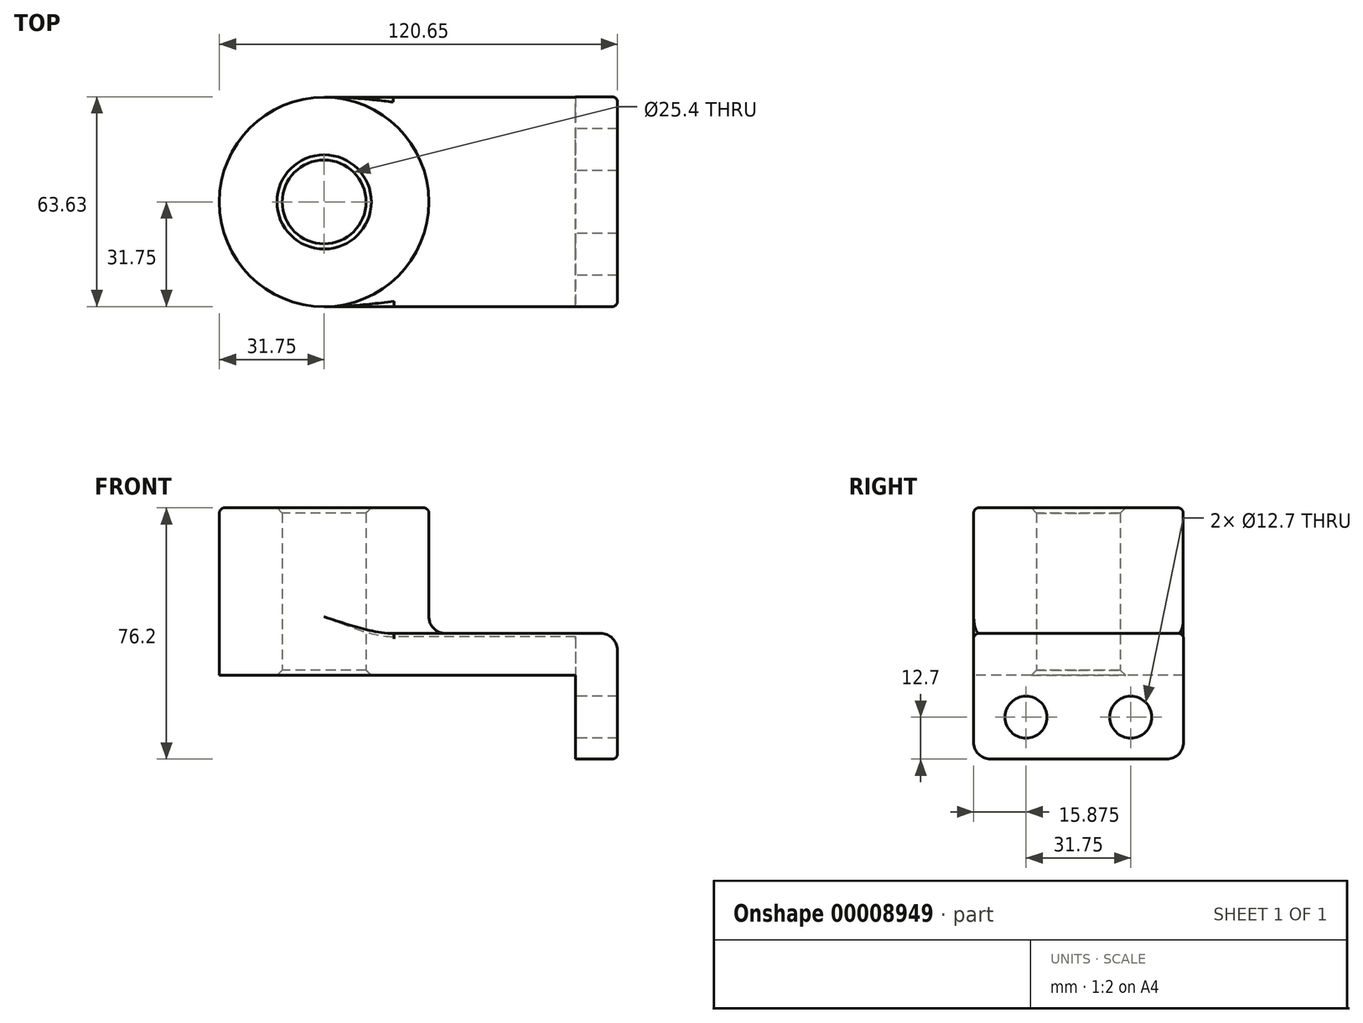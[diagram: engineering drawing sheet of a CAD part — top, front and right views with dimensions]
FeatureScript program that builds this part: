
annotation { "Feature Type Name" : "Feature", "Feature Type Description" : "" }
export const myFeature = defineFeature(function(context is Context, id is Id, definition is map)
    precondition{}
    {
        {
            var Q0;
            Q0=qCreatedBy(makeId("Top.planeOp"),FACE);
            var sketch = newSketch(context, id + "F0", { "sketchPlane" : qUnion([Q0])});
            skLineSegment(sketch, "E0.rect.bottom", {"start": v(-38.1, 31.75) * mm, "end": v(38.1, 31.75) * mm});
            skLineSegment(sketch, "E0.rect.top", {"start": v(-38.1, -31.75) * mm, "end": v(38.1, -31.75) * mm});
            skLineSegment(sketch, "E0.rect.left", {"start": v(-38.1, 31.75) * mm, "end": v(-38.1, -31.75) * mm});
            skLineSegment(sketch, "E0.rect.right", {"start": v(38.1, 31.75) * mm, "end": v(38.1, -31.75) * mm});
            skPoint(sketch, "E0.rect.middle", {"position": v(0, 0) * mm});
            skCircle(sketch, "E1", {"center": v(-38.1, 0) * mm, "radius": 31.75 * mm});
            skCircle(sketch, "E2", {"center": v(-38.1, 0) * mm, "radius": 12.7 * mm});
            skSolve(sketch);
        }
        {
            var Q0;
            {var subQ3=sQuery(id+"F0.wireOp",EDGE,"E0.rect.bottom");Q0=makeQuery(id+"F0.imprint","IMPRINT",FACE,{"disambiguationData":[TD([[makeQuery(id+"F0.imprint","IMPRINT",EDGE,{"derivedFrom":subQ3}),-1.0]])]});}
            var Q1;
            {var subQ0=sQuery(id+"F0.wireOp",EDGE,"E2");var subQ1=sQuery(id+"F0.wireOp",EDGE,"E0.rect.left");var subQ3=makeQuery(id+"F0.imprint","INTERSECT",VERTEX,{"disambiguationData":[OD(0.0)],"derivedFrom":[subQ1,subQ0]});Q1=makeQuery(id+"F0.imprint","IMPRINT",FACE,{"disambiguationData":[TD([[makeQuery(id+"F0.imprint","IMPRINT",EDGE,{"disambiguationData":[TD([[subQ3,1.0]])],"derivedFrom":subQ0}),-1.0]])]});}
            var Q2;
            {var subQ0=sQuery(id+"F0.wireOp",EDGE,"E2");var subQ1=sQuery(id+"F0.wireOp",EDGE,"E0.rect.left");var subQ3=makeQuery(id+"F0.imprint","INTERSECT",VERTEX,{"disambiguationData":[OD(0.0)],"derivedFrom":[subQ1,subQ0]});Q2=makeQuery(id+"F0.imprint","IMPRINT",FACE,{"disambiguationData":[TD([[makeQuery(id+"F0.imprint","IMPRINT",EDGE,{"disambiguationData":[TD([[subQ3,-1.0]])],"derivedFrom":subQ0}),-1.0]])]});}
            extrude(context, id + "F1", {"entities" : qUnion([Q0, Q1, Q2]), "depth" : 12.7 * mm});
        }
        {
            var Q0;
            {var subQ0=sQuery(id+"F0.wireOp",EDGE,"E2");var subQ1=sQuery(id+"F0.wireOp",EDGE,"E0.rect.left");var subQ3=makeQuery(id+"F0.imprint","INTERSECT",VERTEX,{"disambiguationData":[OD(0.0)],"derivedFrom":[subQ1,subQ0]});Q0=makeQuery(id+"F0.imprint","IMPRINT",FACE,{"disambiguationData":[TD([[makeQuery(id+"F0.imprint","IMPRINT",EDGE,{"disambiguationData":[TD([[subQ3,1.0]])],"derivedFrom":subQ0}),-1.0]])]});}
            var Q1;
            {var subQ0=sQuery(id+"F0.wireOp",EDGE,"E2");var subQ1=sQuery(id+"F0.wireOp",EDGE,"E0.rect.left");var subQ3=makeQuery(id+"F0.imprint","INTERSECT",VERTEX,{"disambiguationData":[OD(0.0)],"derivedFrom":[subQ1,subQ0]});Q1=makeQuery(id+"F0.imprint","IMPRINT",FACE,{"disambiguationData":[TD([[makeQuery(id+"F0.imprint","IMPRINT",EDGE,{"disambiguationData":[TD([[subQ3,-1.0]])],"derivedFrom":subQ0}),-1.0]])]});}
            extrude(context, id + "F2", {"entities" : qUnion([Q0, Q1]), "operationType" : NewBodyOperationType.ADD, "depth" : 50.8 * mm});
        }
        {
            var Q0;
            Q0=makeQuery(id+"F1.opExtrude","SWEPT_FACE",FACE,{"disambiguationData":[OSD([sQuery(id+"F0.wireOp",EDGE,"E0.rect.right")])]});
            var sketch = newSketch(context, id + "F3", { "sketchPlane" : qUnion([Q0])});
            skLineSegment(sketch, "E3.bottom", {"start": v(-31.75, 12.7) * mm, "end": v(31.88, 12.7) * mm});
            skLineSegment(sketch, "E3.top", {"start": v(-31.75, -25.4) * mm, "end": v(31.88, -25.4) * mm});
            skLineSegment(sketch, "E3.left", {"start": v(-31.75, 12.7) * mm, "end": v(-31.75, -25.4) * mm});
            skLineSegment(sketch, "E3.right", {"start": v(31.88, 12.7) * mm, "end": v(31.88, -25.4) * mm});
            skLineSegment(sketch, "E4", {"start": v(0, -25.4) * mm, "end": v(0, 0) * mm, "construction": true});
            skCircle(sketch, "E5", {"center": v(-15.87, -12.7) * mm, "radius": 6.35 * mm});
            skCircle(sketch, "E6.MirrorC", {"center": v(15.87, -12.7) * mm, "radius": 6.35 * mm});
            skSolve(sketch);
        }
        {
            var Q0;
            {var subQ5=sQuery(id+"F3.wireOp",EDGE,"E3.top");Q0=makeQuery(id+"F3.imprint","IMPRINT",FACE,{"disambiguationData":[TD([[makeQuery(id+"F3.imprint","IMPRINT",EDGE,{"derivedFrom":subQ5}),1.0]])]});}
            var Q1;
            {var subQ0=sQuery(id+"F0.wireOp",EDGE,"E0.rect.right");var subQ1=makeQuery(id+"F1.opExtrude","CAP_EDGE",EDGE,{"disambiguationData":[OSD([subQ0])],"isStart":true});Q1=makeQuery(id+"F3.imprint","IMPRINT",FACE,{"disambiguationData":[TD([[makeQuery(id+"F3.imprint","IMPRINT",EDGE,{"derivedFrom":subQ1}),-1.0]])]});}
            extrude(context, id + "F4", {"entities" : qUnion([Q0, Q1]), "operationType" : NewBodyOperationType.ADD, "depth" : 12.7 * mm});
        }
        {
            var Q0;
            {var subQ0=sQuery(id+"F0.wireOp",EDGE,"E1");Q0=makeQuery(id+"F2.boolean.opBoolean","INTERSECT",EDGE,{"derivedFrom":[makeQuery(id+"F1.opExtrude","CAP_FACE",FACE,{"disambiguationData":[OSD([sQuery(id+"F0.wireOp",EDGE,"E0.rect.bottom"),sQuery(id+"F0.wireOp",EDGE,"E0.rect.top"),sQuery(id+"F0.wireOp",EDGE,"E0.rect.right"),subQ0,sQuery(id+"F0.wireOp",EDGE,"E2")])],"isStart":false}),makeQuery(id+"F2.opExtrude","SWEPT_FACE",FACE,{"disambiguationData":[OSD([subQ0])]})]});}
            var Q1;
            Q1=makeQuery(id+"F4.opExtrude","SWEPT_EDGE",EDGE,{"disambiguationData":[OSD([sQuery(id+"F3.wireOp",EDGE,"E3.top"),sQuery(id+"F3.wireOp",EDGE,"E3.left")])]});
            var Q2;
            Q2=makeQuery(id+"F4.opExtrude","SWEPT_EDGE",EDGE,{"disambiguationData":[OSD([sQuery(id+"F3.wireOp",EDGE,"E3.top"),sQuery(id+"F3.wireOp",EDGE,"E3.right")])]});
            var Q3;
            Q3=makeQuery(id+"F4.opExtrude","CAP_EDGE",EDGE,{"disambiguationData":[OSD([sQuery(id+"F3.wireOp",EDGE,"E3.bottom")])],"isStart":false});
            var Q4;
            Q4=makeQuery(id+"F1.opExtrude","CAP_EDGE",EDGE,{"disambiguationData":[OSD([sQuery(id+"F0.wireOp",EDGE,"E0.rect.right")])],"isStart":true});
            fillet(context, id + "F5", {"entities" : qUnion([Q0, Q1, Q2, Q3, Q4]), "radius" : 5.08 * mm, "tangentPropagation" : true, "allowEdgeOverflow" : false});
        }
        {
            var Q0;
            Q0=makeQuery(id+"F4.boolean.opBoolean","MERGE",EDGE,{"derivedFrom":[makeQuery(id+"F1.opExtrude","CAP_EDGE",EDGE,{"disambiguationData":[OSD([sQuery(id+"F0.wireOp",EDGE,"E0.rect.top")])],"isStart":false}),makeQuery(id+"F4.opExtrude","SWEPT_EDGE",EDGE,{"disambiguationData":[OSD([sQuery(id+"F3.wireOp",EDGE,"E3.bottom"),sQuery(id+"F3.wireOp",EDGE,"E3.left")])]})]});
            var Q1;
            Q1=makeQuery(id+"F2.opExtrude","CAP_EDGE",EDGE,{"disambiguationData":[OSD([sQuery(id+"F0.wireOp",EDGE,"E1")])],"isStart":false});
            fillet(context, id + "F6", {"entities" : qUnion([Q0, Q1]), "radius" : 1.59 * mm, "tangentPropagation" : true, "allowEdgeOverflow" : false});
        }
        {
            var Q0;
            {var subQ0=sQuery(id+"F0.wireOp",EDGE,"E2");Q0=makeQuery(id+"F2.boolean.opBoolean","MERGE",FACE,{"derivedFrom":[makeQuery(id+"F1.opExtrude","SWEPT_FACE",FACE,{"disambiguationData":[OSD([subQ0])]}),makeQuery(id+"F2.opExtrude","SWEPT_FACE",FACE,{"disambiguationData":[OSD([subQ0])]})]});}
            chamfer(context, id + "F7", {"entities" : qUnion([Q0]), "width" : 1.59 * mm, "tangentPropagation" : true});
        }
    });
